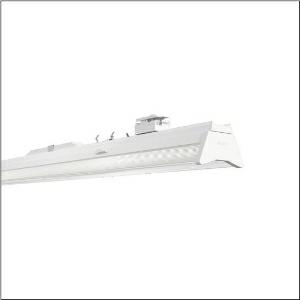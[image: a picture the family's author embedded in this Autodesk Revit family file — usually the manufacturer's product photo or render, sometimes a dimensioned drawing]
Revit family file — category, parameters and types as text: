
# Revit family: licross_r__21_performance_mo_52tm16cn445g_ee6e
name_source: partatom
category: Lighting Fixtures
units: mm (PartAtom-declared; Revit-internal decimal feet)

## family parameters
Cut with Voids When Loaded = No
Host = Face
Light Source = No
Part Type = Normal
Room Calculation Point = No
Round Connector Dimension = Use Diameter
Shared = No

## types (1)
- --- (1 x LED, 4500 lm, 24.1 W, 4000K)
    Apparent Load = 24 VA
    CIE Flux Codes = 66 88 96 79 100
    Color Rendering = 80
    Color Temperature = 4000K
    Default Elevation = 1800 mm
    Description = Licross® 21 Performance MO, luminaire insert, of sheet steel, galvanised, coil coated, white, length: 1.500mm, width: 120mm, height: 123mm, LED rated luminous flux: 4.500lm, light colour: 840, control gear: ON/OFF Multilumen, CLOi, control gear: ECG Multilumen, with plug, 3-pole, with phase selection, mains connection: 220..240V, AC, 50/60Hz, start of lifetime: 24W, end of service life: 28W, halogen-free wiring, primary light control with lens, of plastic, primary optical cover: cover, of PMMA, CAT 2 (L<= 3000cd/m²), light emission: direct/indirect distribution, primary light characteristic: symmetric, protection rating (complete): IP40, insulation class (complete): insulation class I (protective earthing), certification: CE, ENEC, UKCA, protection symbol: D if used in an environment without relevant dust loads with corresponding accessories, impact resistance: IK06, permissible ambient temperature for indoor applications: -35..+55°C, corresponds to IFS (International Featured Standards) requirements for safety and quality in the food industry, reducing of maximum allowable ambient temperature of 5°C with ceiling mounting, LABS conformity tested according to VDMA 24364:2018-05, packaging unit: 1 piece
    Height = 114 mm
    Lamp = 1 x LED
    Lamp Light Flux = 4500 lm
    Lamp Power = 24.1 W
    Lamp count = 1
    Length = 1500 mm
    Luminous efficacy = 187 lm/W
    Manufacturer = Siteco
    ModVariant = No
    Model = 52TM16CN445G
    Mounting Place = Ceiling
    Mounting Type = Pendant
    Number of Poles = 1
    OnlyDefault = Yes
    Power Factor = 1
    Product Name = Licross® 21 Performance MO
    Product group = luminaire insert
    ProductGroupID = 902
    Protection Class = Protection class I
    Protection Degree = IP 40
    RLX_Detail_Level = 1
    RLX_Emergency_Light_Flux = 0 lm
    RLX_Emergency_Type = 0
    RLX_Emergency_Type_DB = No
    RlxData = <blob elided: 31421 chars, md5=73f86dd3>
    Socket = socket
    Standby Power = 0 W
    System Light Flux = 4500 lm
    System Power = 24 W
    Type Comments = factory setting: luminous flux: 100 % | (A | C | E) | 55 mA
    Type Image = l_1256138.jpg
    URL = http://relux.com
    VarID = @adj_049368
    Voltage = 0 V
    Weight = 0.00 kg
    Width = 120 mm

## geometry (parser evidence)
native form markers: Blend x4, Sweep x12
no freeform markers — native parametric forms only
